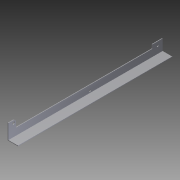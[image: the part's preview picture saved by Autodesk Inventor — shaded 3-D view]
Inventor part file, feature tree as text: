
AUTODESK INVENTOR PART (.ipt)
format: ipt  version: 2012 (Build 160160000, 160)  size: 84,480 bytes
history: native  units: in
note: dims shown in document units (in); Inventor stores cm internally (conversion verified against a paired STEP export)
features: other x3, sketch x1
ambient origin geometry x8: Origin, YZ Plane, XZ Plane, XY Plane, X Axis, Y Axis, Z Axis, Center Point
bodies: Solid1 (feature_tree)
feature tree (4):
  other  "8 ball top roller L frame.ipt"
  other  "Solid1::8 ball top roller L frame.ipt"
  sketch  "Sketch1"  dims[d0=0.3937in]
  other  "TaggingFeature1"
